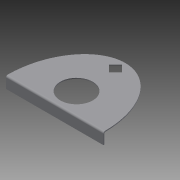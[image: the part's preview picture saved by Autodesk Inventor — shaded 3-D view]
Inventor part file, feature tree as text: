
AUTODESK INVENTOR PART (.ipt)
format: ipt  version: 2015 SP1 (Build 190203100, 203)  size: 115,712 bytes
history: native  units: mm
features: extrude x2, fillet x2, sketch x1
ambient origin geometry x8: Origin, YZ Plane, XZ Plane, XY Plane, X Axis, Y Axis, Z Axis, Center Point
bodies: Body1 (feature_tree)
feature tree (5):
  extrude  "Extrusion3"  Depth=2.0mm
  extrude  "Extrusion4"  Depth=2.0mm
  fillet  "Fillet1"  Radius=45.0mm
  fillet  "Fillet2"  Radius=115.0mm
  sketch  "Sketch2"  dims[d0=105.0mm d1=20.0mm d2=20.0mm d26=45.0mm d29=115.0mm d32=70.0mm d33=150.0mm d34=2.0mm d35=0.0mm d36=2.0mm d37=25.0mm d38=0.0mm d39=4.0mm d40=2.0mm]
